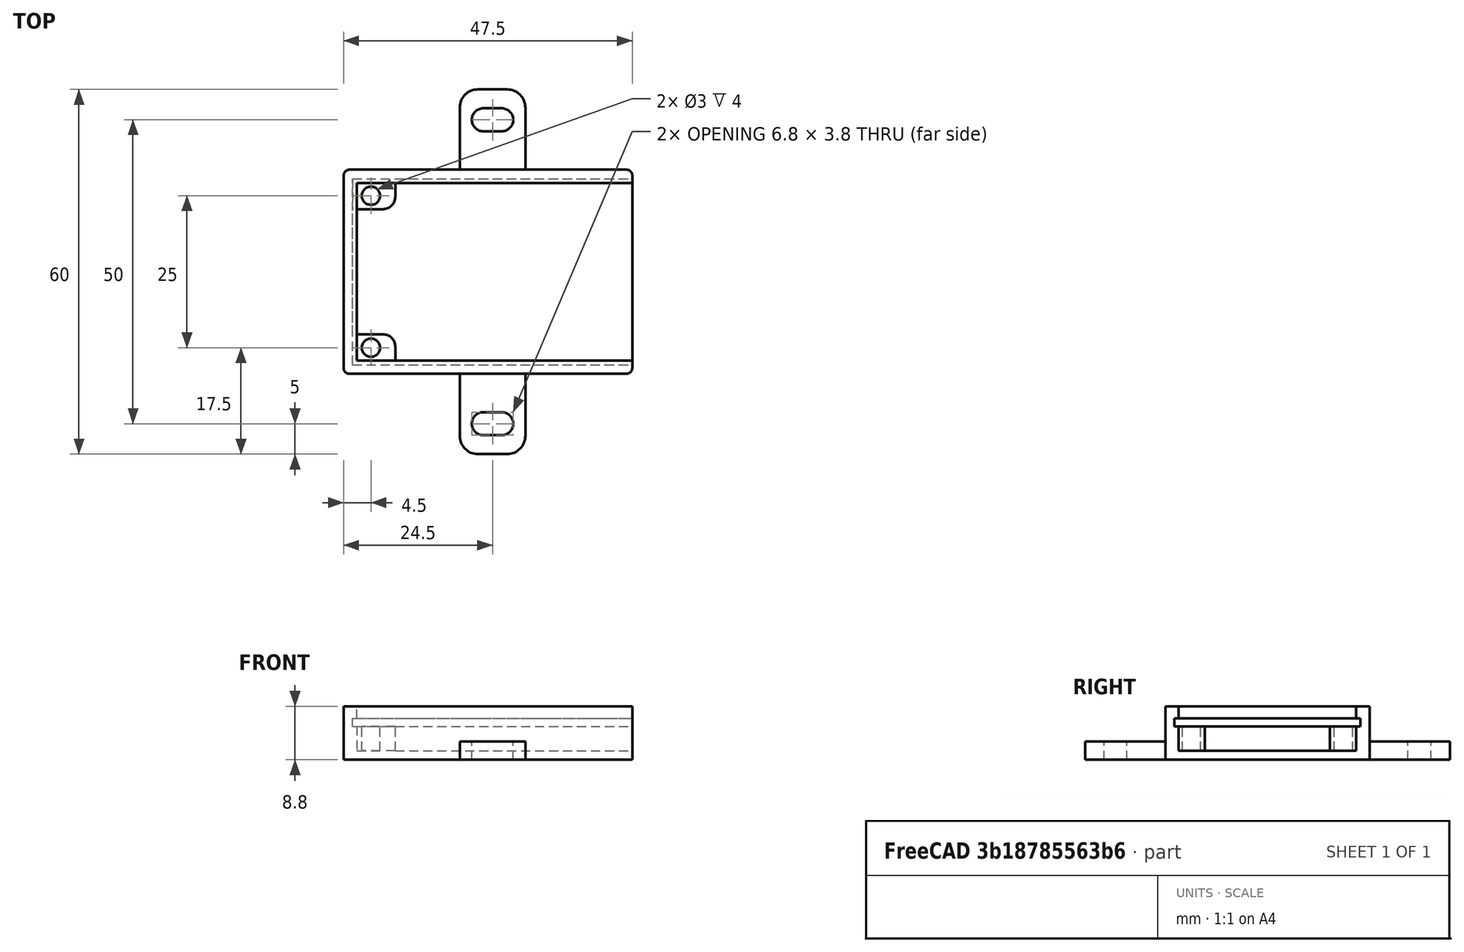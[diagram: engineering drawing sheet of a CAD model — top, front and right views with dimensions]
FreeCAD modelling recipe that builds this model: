
FCSTD DOCUMENT  (FreeCAD 0.18.4R)
Label: sd_card
License: FreeArt
LicenseURL: http://artlibre.org/licence/lal
objects: Part::Box×4, Part::MultiFuse×4, Part::Fillet×2, Part::Cut×2, Spreadsheet::Sheet×1, Part::Feature×1, Part::Cylinder×1, Part::Mirroring×1, App::Part×1
note: 15 computed .brp shape members not serialized (recipe doc carries the construction recipe); baked Part::Feature solids carry a one-line shape summary decoded from their .brp

FEATURE [Spreadsheet::Sheet] Spreadsheet  label="p"
  cells = A1=pcb_x; B1(pcb_x)=46; A2=pcb_y; B2(pcb_y)=30.6; A3=pcb_z; B3(pcb_z)=1.3; A4=pcb_under; B4(pcb_under)=4; A5=side_wall; B5(side_wall)=1.5; A6=pcb_side_lane; B6(pcb_side_lane)=0.7; A7=bottom_wall; B7(bottom_wall)=1.5; A8=pcb_above; B8(pcb_above)=2; A9=hole_dist_y; B9(hole_dist_y)=25; A10=hole_off_x; B10(hole_off_x)=3; A11=hole_r; B11(hole_r)=1.5; A12=hole_stand_x; B12(hole_stand_x)=7; A13=hole_stand_y; B13(hole_stand_y)=5
FEATURE [Part::Box] Box  label="external cube"
  AttacherType = Attacher::AttachEngine3D
  Height = 8.8
  Length = 47.5
  Width = 33.6
  expr: Height = p.bottom_wall + p.pcb_under + p.pcb_z + p.pcb_above
  expr: Width = p.pcb_y + 2 * p.side_wall
  expr: Length = p.pcb_x + p.side_wall
FEATURE [Part::Box] Box006  label="internal cube"
  AttacherType = Attacher::AttachEngine3D
  Height = 7.3
  Length = 46.1
  Placement = pos=(2.2,2.2,1.5) rot=(0,0,1;0rad)
  Width = 29.2
  expr: Placement.Base.y = p.side_wall + p.pcb_side_lane
  expr: Placement.Base.x = p.side_wall + p.pcb_side_lane
  expr: Placement.Base.z = p.bottom_wall
  expr: Height = p.pcb_under + p.pcb_z + p.pcb_above
  expr: Width = p.pcb_y - 2 * p.pcb_side_lane
  expr: Length = p.pcb_x - 2 * p.pcb_side_lane + p.side_wall
FEATURE [Part::Box] Box007  label="pcb extract cube"
  AttacherType = Attacher::AttachEngine3D
  Height = 1.3
  Length = 46
  Placement = pos=(1.5,1.5,5.5) rot=(0,0,1;0rad)
  Width = 30.6
  expr: Placement.Base.y = p.side_wall
  expr: Placement.Base.x = p.side_wall
  expr: Length = p.pcb_x
  expr: Width = p.pcb_y
  expr: Placement.Base.z = p.bottom_wall + p.pcb_under
  expr: Height = p.pcb_z
FEATURE [Part::MultiFuse] Fusion  label="extract fusion"
  Shapes = -> [Box006,Box007]
FEATURE [Part::Fillet] Fillet  label="external fillet"
  Base = -> Box
  Edges = 4 edges r=1: [Edge1,Edge3,Edge5,Edge7]
FEATURE [Part::Feature] Cut002002  label="attach plane y dir002"
  shape: bbox 10.8 x 60 x 3 mm, 18 faces (baked)
FEATURE [Part::MultiFuse] Fusion001  label="solid fusion"
  Shapes = -> [Fillet,Cut002002]
FEATURE [Part::Cut] Cut  label="sd card cut"
  Base = -> Fusion001
  Tool = -> Fusion
FEATURE [Part::Box] Box008  label="hole stand"
  AttacherType = Attacher::AttachEngine3D
  Height = 4
  Length = 7
  Placement = pos=(1.5,1.5,1.5) rot=(0,0,1;0rad)
  Width = 5
  expr: Placement.Base.x = p.side_wall
  expr: Placement.Base.y = p.side_wall
  expr: Length = p.hole_stand_x
  expr: Width = p.hole_stand_y
  expr: Placement.Base.z = p.bottom_wall
  expr: Height = p.pcb_under
FEATURE [Part::Cylinder] Cylinder  label="hole"
  Angle = 360
  AttacherType = Attacher::AttachEngine3D
  Height = 10
  Placement = pos=(4.5,4.3,0) rot=(0,0,1;0rad)
  Radius = 1.5
  expr: Placement.Base.y = p.side_wall + (p.pcb_y - p.hole_dist_y) / 2
  expr: Placement.Base.x = p.hole_off_x + p.side_wall
  expr: Radius = p.hole_r
FEATURE [Part::Fillet] Fillet001  label="hole stand fillet"
  Base = -> Box008
  Edges = 1 edges r=2: [Edge7]
FEATURE [Part::Cut] Cut002003  label="hole cut"
  Base = -> Fillet001
  Tool = -> Cylinder
FEATURE [Part::Mirroring] Part__Mirroring  label="hole stand (Mirror #1)"
  Base = (0,16.8,0)
  Normal = (0,1,0)
  Source = -> Cut002003
  expr: Base.y = p.pcb_y / 2 + p.side_wall
FEATURE [Part::MultiFuse] Fusion002  label="hole fusion"
  Shapes = -> [Cut002003,Part__Mirroring]
FEATURE [Part::MultiFuse] Fusion003  label="sd card fusion"
  Shapes = -> [Fusion002,Cut]
FEATURE [App::Part] Part  label="sd card pcb box part"
  Group = -> [Box,Fillet,Fusion001,Fusion,Box007,Box006,Cut,Part__Mirroring,Cut002003,Fusion002,Box008,Cut002002,Fillet001,Cylinder,Fusion003]
  Origin = -> Origin
